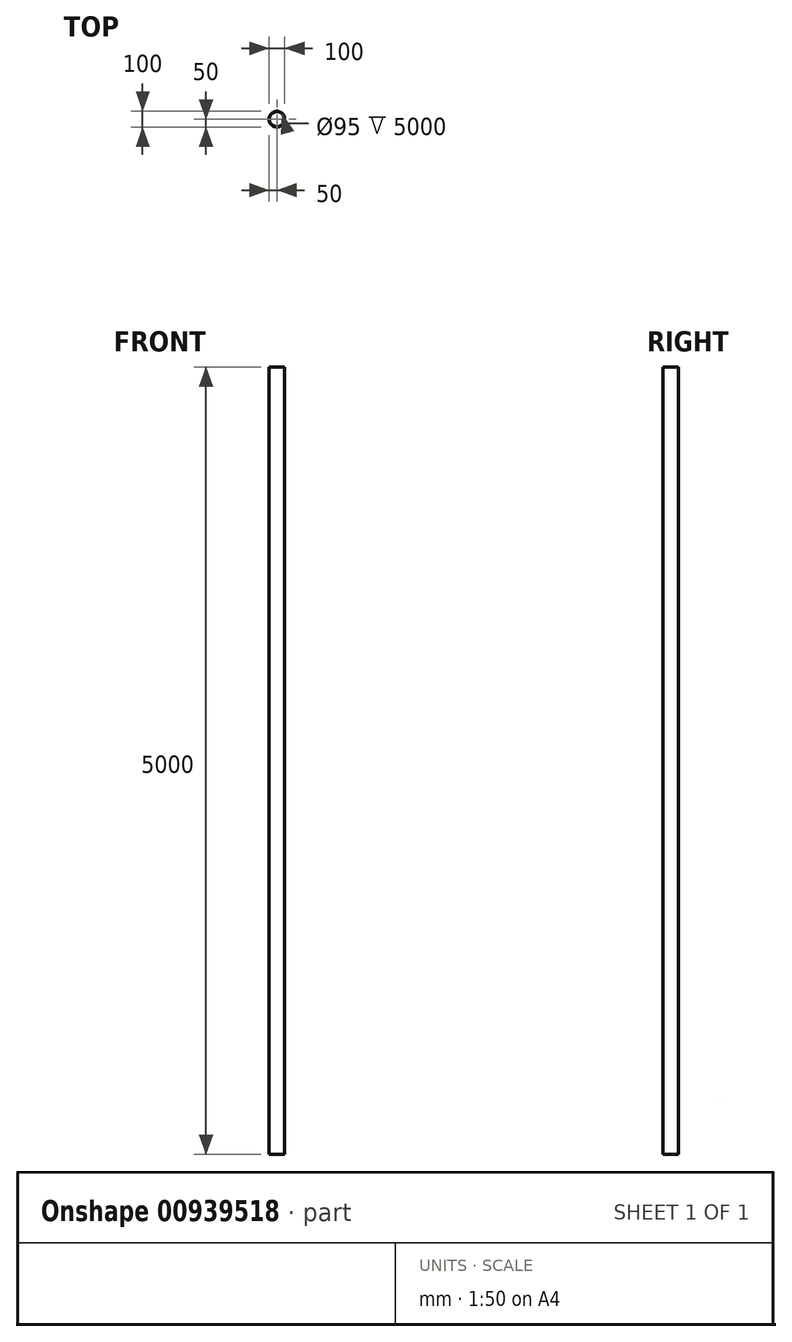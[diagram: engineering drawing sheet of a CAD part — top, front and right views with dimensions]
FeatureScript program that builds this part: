
annotation { "Feature Type Name" : "Feature", "Feature Type Description" : "" }
export const myFeature = defineFeature(function(context is Context, id is Id, definition is map)
    precondition{}
    {
        {
            var Q0;
            Q0=qCreatedBy(makeId("Top.planeOp"),FACE);
            var sketch = newSketch(context, id + "F0", { "sketchPlane" : qUnion([Q0])});
            skCircle(sketch, "E0", {"center": v(0, 0) * mm, "radius": 50 * mm});
            skSolve(sketch);
        }
        {
            var Q0;
            Q0 = qSketchRegion(id + "F0", true);
            extrude(context, id + "F1", {"entities" : qUnion([Q0]), "depth" : 5000 * mm, "offsetDistance" : 25 * mm});
        }
        {
            var Q0;
            Q0=makeQuery(id+"F1.opExtrude","CAP_FACE",FACE,{"disambiguationData":[OSD([sQuery(id+"F0.wireOp",EDGE,"E0")])],"isStart":false});
            var Q1;
            Q1=makeQuery(id+"F1.opExtrude","CAP_FACE",FACE,{"disambiguationData":[OSD([sQuery(id+"F0.wireOp",EDGE,"E0")])],"isStart":true});
            var Q2;
            Q2=makeQuery(id+"F1.opExtrude","SWEPT_BODY",BODY,{"disambiguationData":[OSD([sQuery(id+"F0.wireOp",EDGE,"E0")])]});
            shell(context, id + "F2", {"entities" : qUnion([Q0, Q1]), "parts" : qUnion([Q2]), "thickness" : 2.5 * mm});
        }
    });
